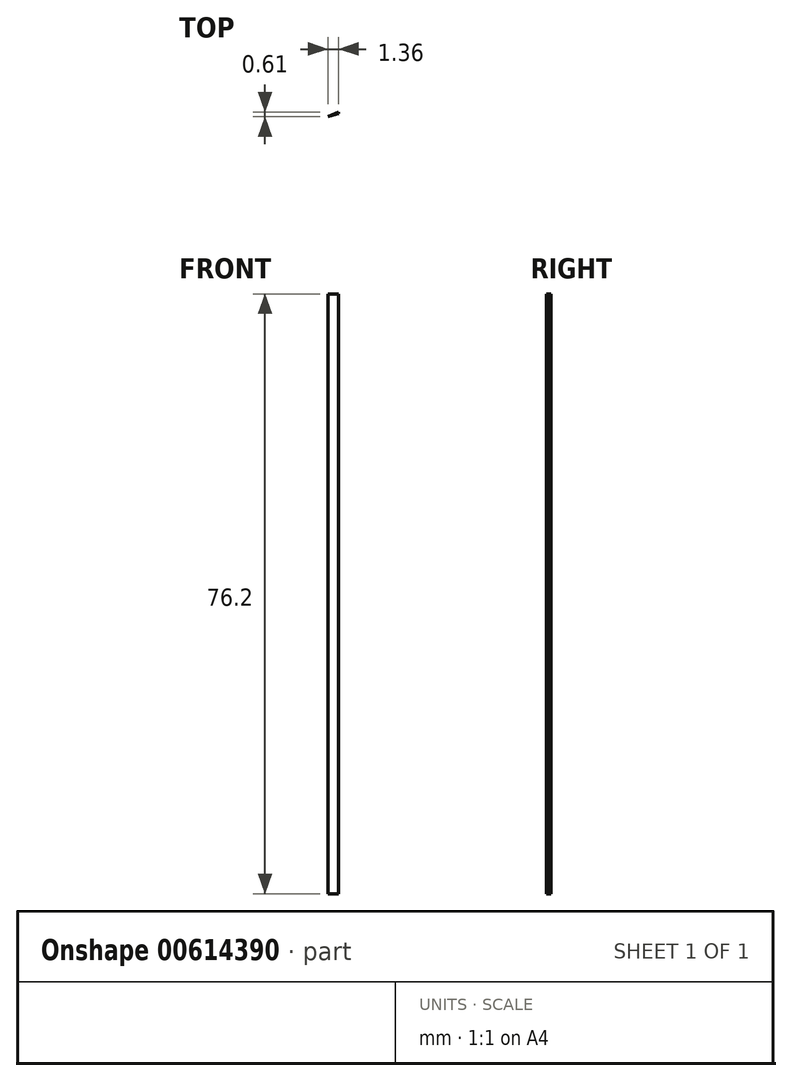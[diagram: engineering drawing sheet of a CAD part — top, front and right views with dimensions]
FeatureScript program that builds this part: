
annotation { "Feature Type Name" : "Feature", "Feature Type Description" : "" }
export const myFeature = defineFeature(function(context is Context, id is Id, definition is map)
    precondition{}
    {
        {
            var Q0;
            Q0=qCreatedBy(makeId("Top.planeOp"),FACE);
            var sketch = newSketch(context, id + "F0", { "sketchPlane" : qUnion([Q0])});
            skLineSegment(sketch, "E0.bottom", {"start": v(-54.4, 71.53) * mm, "end": v(47.2, 71.53) * mm});
            skLineSegment(sketch, "E0.top", {"start": v(-54.4, -4.67) * mm, "end": v(47.2, -4.67) * mm});
            skLineSegment(sketch, "E0.left", {"start": v(-54.4, 71.53) * mm, "end": v(-54.4, -4.67) * mm});
            skLineSegment(sketch, "E0.right", {"start": v(47.2, 71.53) * mm, "end": v(47.2, -4.67) * mm});
            skLineSegment(sketch, "E1", {"start": v(46.22, 71.54) * mm, "end": v(72.42, 71.73) * mm});
            skLineSegment(sketch, "E2", {"start": v(72.42, 71.73) * mm, "end": v(91.4, 71.93) * mm});
            skLineSegment(sketch, "E3", {"start": v(91.4, 71.93) * mm, "end": v(45.83, 51.59) * mm});
            skLineSegment(sketch, "E4", {"start": v(45.83, 51.59) * mm, "end": v(47.2, 51.98) * mm});
            skLineSegment(sketch, "E5", {"start": v(47.2, 51.98) * mm, "end": v(45.83, 51.78) * mm});
            skLineSegment(sketch, "E6", {"start": v(45.83, 51.78) * mm, "end": v(46.22, 1.32) * mm});
            skLineSegment(sketch, "E7", {"start": v(53.2, 1.32) * mm, "end": v(53.01, -0.24) * mm});
            skLineSegment(sketch, "E8", {"start": v(47.52, -5.72) * mm, "end": v(90.17, -5.72) * mm});
            skLineSegment(sketch, "E9", {"start": v(90.17, -5.72) * mm, "end": v(47.34, 13.45) * mm});
            skSolve(sketch);
        }
        {
            var Q0;
            {var subQ1=sQuery(id+"F0.wireOp",EDGE,"E0.right");var subQ3=sQuery(id+"F0.wireOp",EDGE,"E3");var subQ4=makeQuery(id+"F0.imprint","INTERSECT",VERTEX,{"derivedFrom":[subQ1,subQ3]});Q0=makeQuery(id+"F0.imprint","IMPRINT",FACE,{"disambiguationData":[TD([[makeQuery(id+"F0.imprint","IMPRINT",EDGE,{"disambiguationData":[TD([[subQ4,-1.0]])],"derivedFrom":subQ3}),1.0]])]});}
            var Q1;
            {var subQ0=sQuery(id+"F0.wireOp",EDGE,"E5");var subQ1=sQuery(id+"F0.wireOp",EDGE,"E3");var subQ2=makeQuery(id+"F0.imprint","INTERSECT",VERTEX,{"derivedFrom":[subQ1,subQ0]});Q1=makeQuery(id+"F0.imprint","IMPRINT",FACE,{"disambiguationData":[TD([[makeQuery(id+"F0.imprint","IMPRINT",EDGE,{"disambiguationData":[TD([[subQ2,-1.0]])],"derivedFrom":subQ1}),1.0]])]});}
            extrude(context, id + "F1", {"entities" : qUnion([Q0, Q1]), "depth" : 76.2 * mm, "offsetDistance" : 25.4 * mm});
        }
    });
